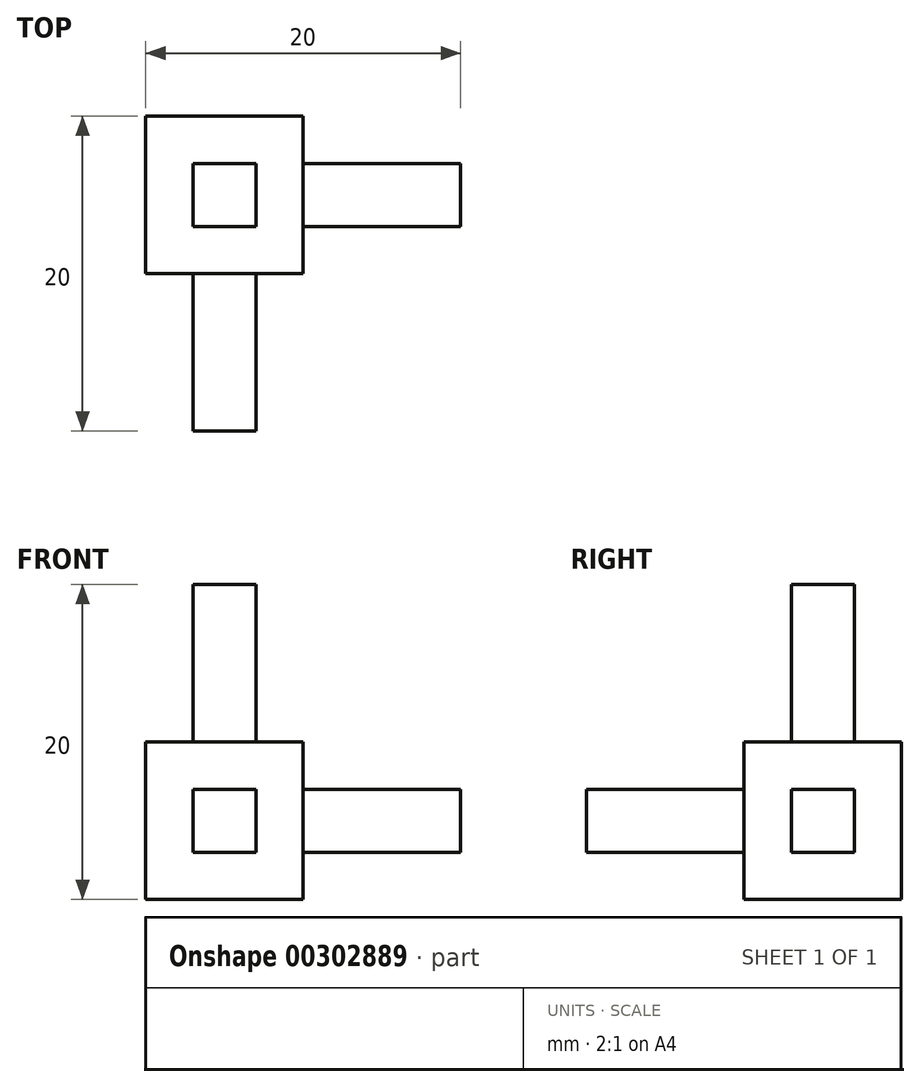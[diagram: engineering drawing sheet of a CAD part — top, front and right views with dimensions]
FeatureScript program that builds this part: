
annotation { "Feature Type Name" : "Feature", "Feature Type Description" : "" }
export const myFeature = defineFeature(function(context is Context, id is Id, definition is map)
    precondition{}
    {
        {
            var Q0;
            Q0=qCreatedBy(makeId("Top.planeOp"),FACE);
            var sketch = newSketch(context, id + "F0", { "sketchPlane" : qUnion([Q0])});
            skLineSegment(sketch, "E0.bottom", {"start": v(-5, 5) * mm, "end": v(5, 5) * mm});
            skLineSegment(sketch, "E0.top", {"start": v(-5, -5) * mm, "end": v(5, -5) * mm});
            skLineSegment(sketch, "E0.left", {"start": v(-5, 5) * mm, "end": v(-5, -5) * mm});
            skLineSegment(sketch, "E0.right", {"start": v(5, 5) * mm, "end": v(5, -5) * mm});
            skPoint(sketch, "E0.middle", {"position": v(0, 0) * mm});
            skSolve(sketch);
        }
        {
            var Q0;
            Q0 = qSketchRegion(id + "F0", true);
            extrude(context, id + "F1", {"entities" : qUnion([Q0]), "endBound" : BoundingType.SYMMETRIC, "depth" : 10 * mm});
        }
        {
            var Q0;
            Q0=qCreatedBy(makeId("Top.planeOp"),FACE);
            var sketch = newSketch(context, id + "F2", { "sketchPlane" : qUnion([Q0])});
            skLineSegment(sketch, "E1.bottom", {"start": v(-2, 2) * mm, "end": v(2, 2) * mm});
            skLineSegment(sketch, "E1.top", {"start": v(-2, -2) * mm, "end": v(2, -2) * mm});
            skLineSegment(sketch, "E1.left", {"start": v(-2, 2) * mm, "end": v(-2, -2) * mm});
            skLineSegment(sketch, "E1.right", {"start": v(2, 2) * mm, "end": v(2, -2) * mm});
            skPoint(sketch, "E1.middle", {"position": v(0, 0) * mm});
            skSolve(sketch);
        }
        {
            var Q0;
            Q0 = qSketchRegion(id + "F2", true);
            extrude(context, id + "F3", {"entities" : qUnion([Q0]), "operationType" : NewBodyOperationType.ADD, "depth" : 15 * mm});
        }
        {
            var Q0;
            Q0=qCreatedBy(makeId("Front.planeOp"),FACE);
            var sketch = newSketch(context, id + "F4", { "sketchPlane" : qUnion([Q0])});
            skLineSegment(sketch, "E2.bottom", {"start": v(2, 2) * mm, "end": v(-2, 2) * mm});
            skLineSegment(sketch, "E2.top", {"start": v(2, -2) * mm, "end": v(-2, -2) * mm});
            skLineSegment(sketch, "E2.left", {"start": v(2, 2) * mm, "end": v(2, -2) * mm});
            skLineSegment(sketch, "E2.right", {"start": v(-2, 2) * mm, "end": v(-2, -2) * mm});
            skPoint(sketch, "E2.middle", {"position": v(0, 0) * mm});
            skSolve(sketch);
        }
        {
            var Q0;
            Q0 = qSketchRegion(id + "F4", true);
            extrude(context, id + "F5", {"entities" : qUnion([Q0]), "operationType" : NewBodyOperationType.ADD, "depth" : 15 * mm});
        }
        {
            var Q0;
            Q0=qCreatedBy(makeId("Right.planeOp"),FACE);
            var sketch = newSketch(context, id + "F6", { "sketchPlane" : qUnion([Q0])});
            skLineSegment(sketch, "E3.bottom", {"start": v(-2, 2) * mm, "end": v(2, 2) * mm});
            skLineSegment(sketch, "E3.top", {"start": v(-2, -2) * mm, "end": v(2, -2) * mm});
            skLineSegment(sketch, "E3.left", {"start": v(-2, 2) * mm, "end": v(-2, -2) * mm});
            skLineSegment(sketch, "E3.right", {"start": v(2, 2) * mm, "end": v(2, -2) * mm});
            skPoint(sketch, "E3.middle", {"position": v(0, 0) * mm});
            skSolve(sketch);
        }
        {
            var Q0;
            Q0 = qSketchRegion(id + "F6", true);
            extrude(context, id + "F7", {"entities" : qUnion([Q0]), "operationType" : NewBodyOperationType.ADD, "depth" : 15 * mm});
        }
    });
